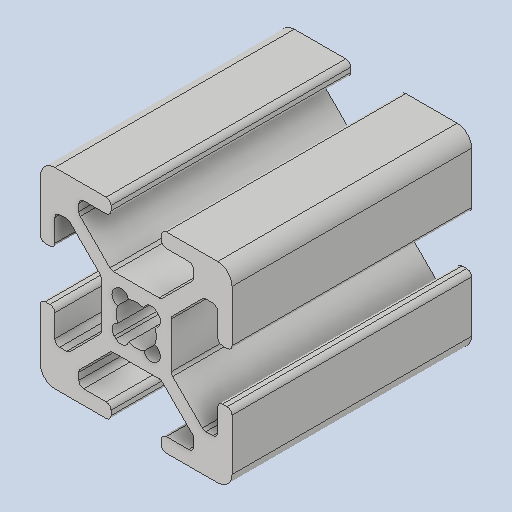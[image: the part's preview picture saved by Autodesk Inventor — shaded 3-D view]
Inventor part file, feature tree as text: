
AUTODESK INVENTOR PART (.ipt)
format: ipt  version: 2023 (Build 270158000, 158)  size: 275,968 bytes
history: native  units: mm
features: plane x2, extrude x1, sketch x1
ambient origin geometry x8: Origin, YZ Plane, XZ Plane, XY Plane, X Axis, Y Axis, Z Axis, Center Point
bodies: Solid1 (feature_tree)
feature tree (4):
  extrude  "Extrusion1"  [1 undecoded]
  plane  "Work Plane1"
  plane  "Work Plane2"
  sketch  "Sketch_1"  dims[d0=25.0mm d1=0.0mm]
note: 1 required parameter value undecoded (feature->parameter linkage not recoverable at this tier; creation-order binding heuristic only, values carry confidence <= 0.55)
